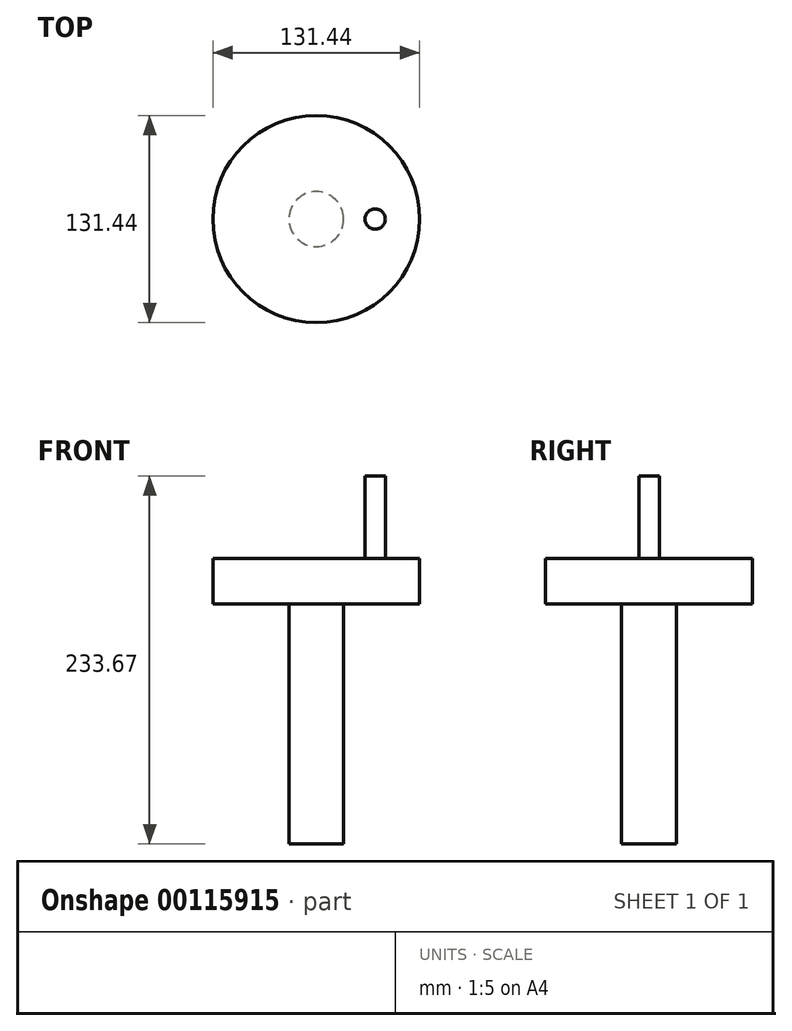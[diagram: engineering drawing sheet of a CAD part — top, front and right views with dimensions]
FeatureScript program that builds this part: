
annotation { "Feature Type Name" : "Feature", "Feature Type Description" : "" }
export const myFeature = defineFeature(function(context is Context, id is Id, definition is map)
    precondition{}
    {
        {
            var Q0;
            Q0=qCreatedBy(makeId("Top.planeOp"),FACE);
            var sketch = newSketch(context, id + "F0", { "sketchPlane" : qUnion([Q0])});
            skCircle(sketch, "E0", {"center": v(0, 0) * mm, "radius": 65.72 * mm});
            skSolve(sketch);
        }
        {
            var Q0;
            Q0 = qSketchRegion(id + "F0", true);
            extrude(context, id + "F1", {"entities" : qUnion([Q0]), "oppositeDirection" : true, "depth" : 28.96 * mm});
        }
        {
            var Q0;
            Q0=qCreatedBy(makeId("Top.planeOp"),FACE);
            var sketch = newSketch(context, id + "F2", { "sketchPlane" : qUnion([Q0])});
            skCircle(sketch, "E1", {"center": v(37.4, 0) * mm, "radius": 6.44 * mm});
            skSolve(sketch);
        }
        {
            var Q0;
            Q0 = qSketchRegion(id + "F2", true);
            extrude(context, id + "F3", {"entities" : qUnion([Q0]), "operationType" : NewBodyOperationType.ADD, "depth" : 52.36 * mm});
        }
        {
            var Q0;
            Q0=makeQuery(id+"F1.opExtrude","CAP_FACE",FACE,{"disambiguationData":[OSD([sQuery(id+"F0.wireOp",EDGE,"E0")])],"isStart":false});
            var sketch = newSketch(context, id + "F4", { "sketchPlane" : qUnion([Q0])});
            skCircle(sketch, "E2", {"center": v(0, 0) * mm, "radius": 17.45 * mm});
            skSolve(sketch);
        }
        {
            var Q0;
            Q0=makeQuery(id+"F4.imprint","IMPRINT",FACE,{"disambiguationData":[TD([[makeQuery(id+"F4.imprint","IMPRINT",EDGE,{"derivedFrom":sQuery(id+"F4.wireOp",EDGE,"E2")}),1.0]])]});
            var Q1;
            Q1 = qSketchRegion(id + "F4", true);
            extrude(context, id + "F5", {"entities" : qUnion([Q0, Q1]), "operationType" : NewBodyOperationType.ADD, "depth" : 152.36 * mm});
        }
    });
